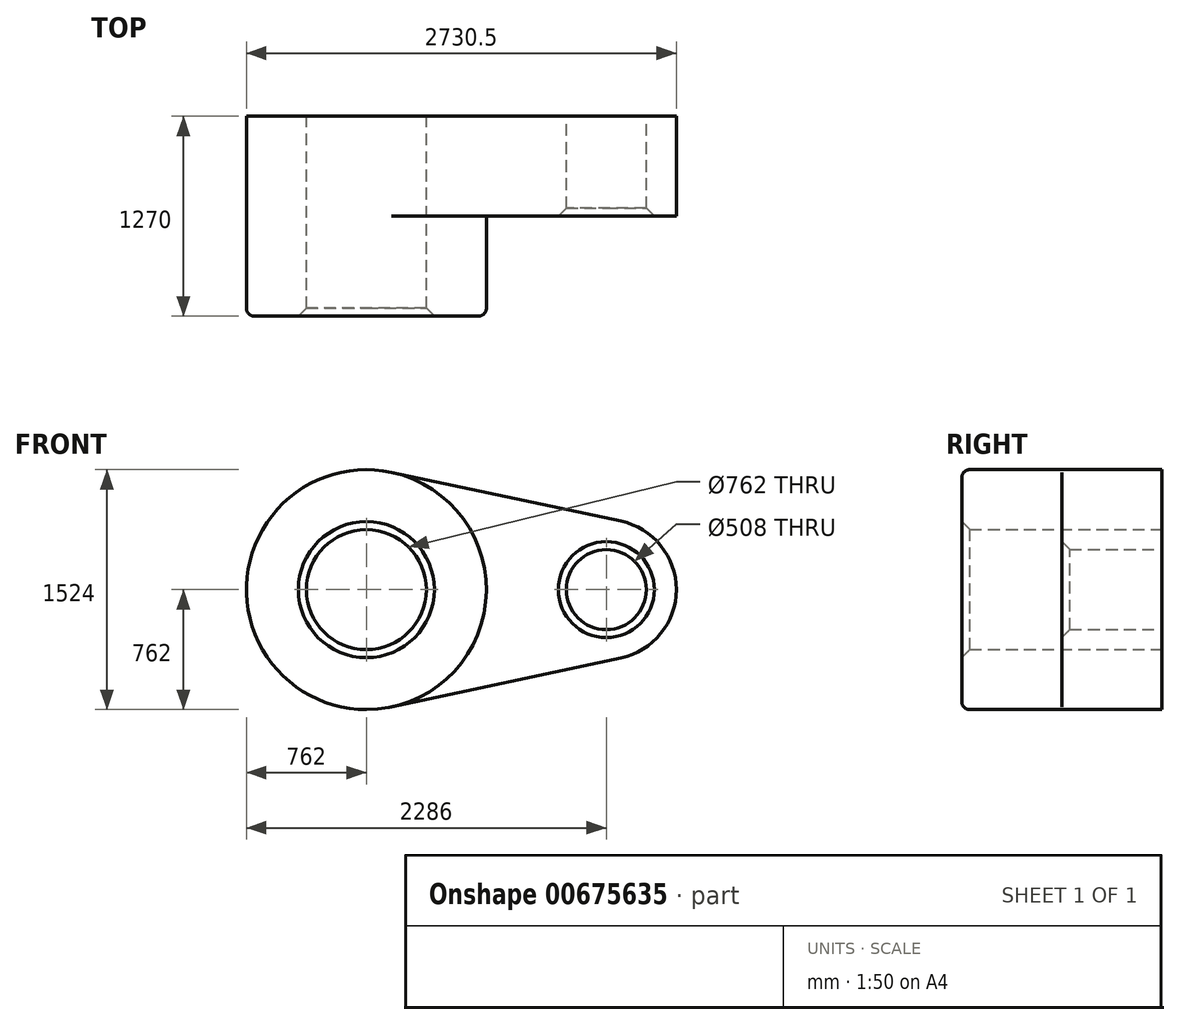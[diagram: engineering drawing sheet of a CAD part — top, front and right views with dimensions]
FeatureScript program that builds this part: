
annotation { "Feature Type Name" : "Feature", "Feature Type Description" : "" }
export const myFeature = defineFeature(function(context is Context, id is Id, definition is map)
    precondition{}
    {
        {
            var Q0;
            Q0=qCreatedBy(makeId("Front.planeOp"),FACE);
            var sketch = newSketch(context, id + "F0", { "sketchPlane" : qUnion([Q0])});
            skCircle(sketch, "E0", {"center": v(0, 0) * mm, "radius": 762 * mm});
            skCircle(sketch, "E1", {"center": v(1524, 0) * mm, "radius": 444.5 * mm});
            skLineSegment(sketch, "E2", {"start": v(158.75, 745.28) * mm, "end": v(1616.6, 434.75) * mm});
            skLineSegment(sketch, "E3", {"start": v(158.75, -745.28) * mm, "end": v(1616.6, -434.75) * mm});
            skCircle(sketch, "E4", {"center": v(1524, 0) * mm, "radius": 254 * mm});
            skCircle(sketch, "E5", {"center": v(0, 0) * mm, "radius": 381 * mm});
            skSolve(sketch);
        }
        {
            var Q0;
            Q0 = qSketchRegion(id + "F0", true);
            extrude(context, id + "F1", {"entities" : qUnion([Q0]), "depth" : 635 * mm, "offsetDistance" : 25.4 * mm});
        }
        {
            var Q0;
            Q0=makeQuery(id+"F0.imprint","IMPRINT",FACE,{"disambiguationData":[TD([[makeQuery(id+"F0.imprint","IMPRINT",EDGE,{"derivedFrom":sQuery(id+"F0.wireOp",EDGE,"E5")}),-1.0]])]});
            extrude(context, id + "F2", {"entities" : qUnion([Q0]), "operationType" : NewBodyOperationType.ADD, "depth" : 1270 * mm, "offsetDistance" : 25.4 * mm});
        }
        {
            var Q0;
            Q0=makeQuery(id+"F2.opExtrude","CAP_EDGE",EDGE,{"disambiguationData":[OSD([sQuery(id+"F0.wireOp",EDGE,"E0")])],"isStart":false});
            fillet(context, id + "F3", {"entities" : qUnion([Q0]), "radius" : 50.8 * mm, "tangentPropagation" : true, "allowEdgeOverflow" : false});
        }
        {
            var Q0;
            Q0=makeQuery(id+"F2.opExtrude","CAP_EDGE",EDGE,{"disambiguationData":[OSD([sQuery(id+"F0.wireOp",EDGE,"E5")])],"isStart":false});
            var Q1;
            Q1=makeQuery(id+"F1.opExtrude","CAP_EDGE",EDGE,{"disambiguationData":[OSD([sQuery(id+"F0.wireOp",EDGE,"E4")])],"isStart":false});
            chamfer(context, id + "F4", {"entities" : qUnion([Q0, Q1]), "width" : 50.8 * mm, "tangentPropagation" : true});
        }
    });
